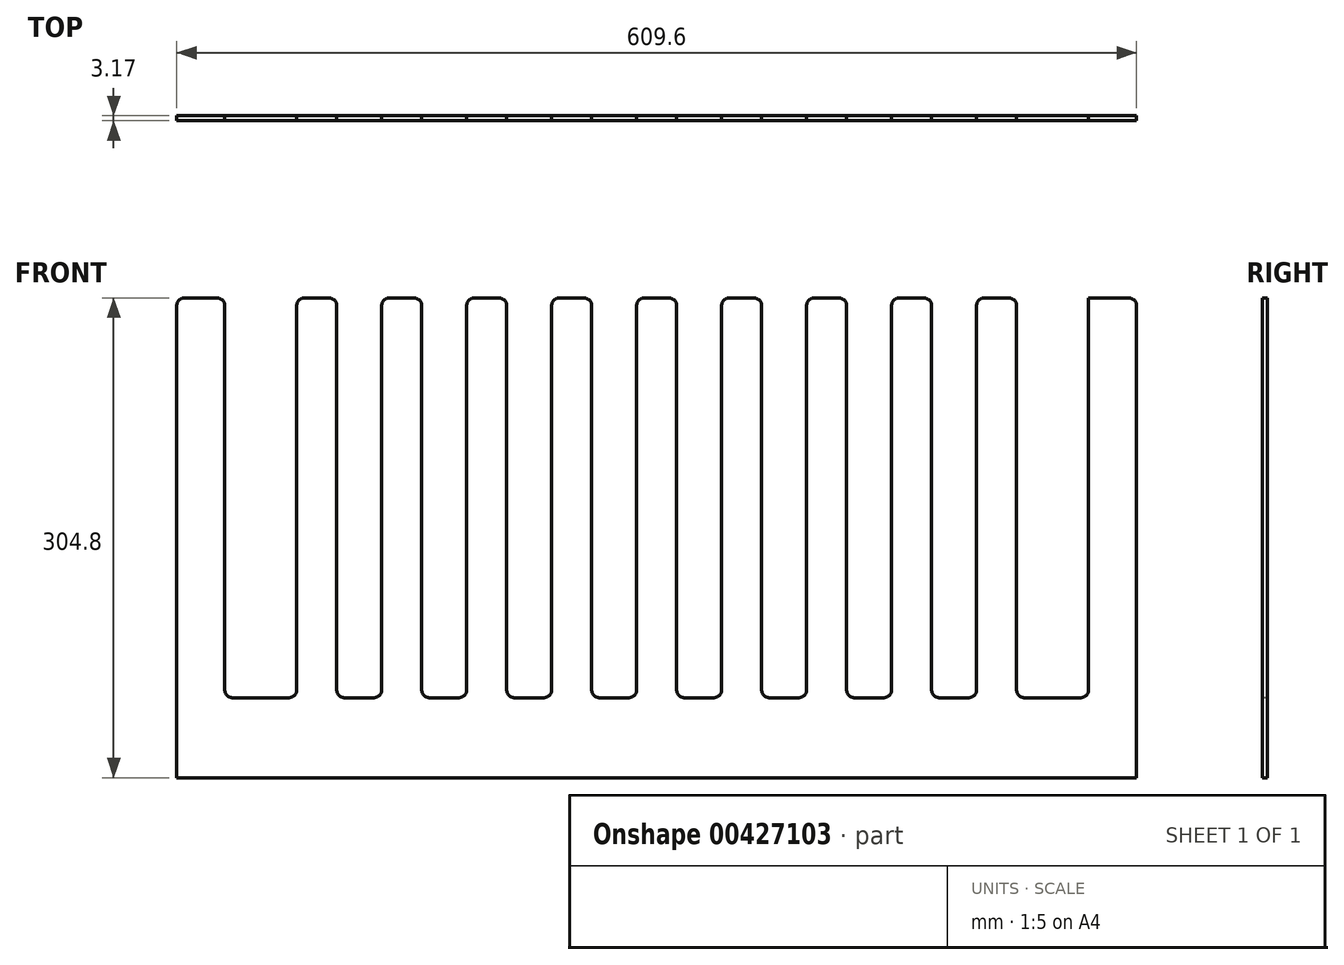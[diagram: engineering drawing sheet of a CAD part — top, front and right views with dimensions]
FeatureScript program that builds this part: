
annotation { "Feature Type Name" : "Feature", "Feature Type Description" : "" }
export const myFeature = defineFeature(function(context is Context, id is Id, definition is map)
    precondition{}
    {
        {
            var Q0;
            Q0=qCreatedBy(makeId("Front.planeOp"),FACE);
            var sketch = newSketch(context, id + "F0", { "sketchPlane" : qUnion([Q0])});
            skLineSegment(sketch, "E0.bottom", {"start": v(304.8, -152.4) * mm, "end": v(-304.8, -152.4) * mm});
            skLineSegment(sketch, "E0.top", {"start": v(304.8, 152.4) * mm, "end": v(-304.8, 152.4) * mm});
            skLineSegment(sketch, "E0.left", {"start": v(304.8, -152.4) * mm, "end": v(304.8, 152.4) * mm});
            skLineSegment(sketch, "E0.right", {"start": v(-304.8, -152.4) * mm, "end": v(-304.8, 152.4) * mm});
            skPoint(sketch, "E0.middle", {"position": v(0, 0) * mm});
            skSolve(sketch);
        }
        {
            var Q0;
            Q0=makeQuery(id+"F0.imprint","IMPRINT",FACE,{"disambiguationData":[TD([[makeQuery(id+"F0.imprint","IMPRINT",EDGE,{"derivedFrom":sQuery(id+"F0.wireOp",EDGE,"E0.bottom")}),-1.0]])]});
            extrude(context, id + "F1", {"entities" : qUnion([Q0]), "depth" : 3.17 * mm, "offsetDistance" : 25.4 * mm});
        }
        {
            var Q0;
            Q0=makeQuery(id+"F1.opExtrude","SWEPT_FACE",FACE,{"disambiguationData":[OSD([sQuery(id+"F0.wireOp",EDGE,"E0.top")])]});
            var sketch = newSketch(context, id + "F2", { "sketchPlane" : qUnion([Q0])});
            skLineSegment(sketch, "E1.bottom", {"start": v(-304.8, 0) * mm, "end": v(-274.32, 0) * mm});
            skLineSegment(sketch, "E1.top", {"start": v(-304.8, -3.18) * mm, "end": v(-274.32, -3.17) * mm});
            skLineSegment(sketch, "E1.left", {"start": v(-304.8, 0) * mm, "end": v(-304.8, -3.18) * mm});
            skLineSegment(sketch, "E1.right", {"start": v(-274.32, 0) * mm, "end": v(-274.32, -3.18) * mm});
            skLineSegment(sketch, "E2.bottom", {"start": v(-274.32, 0) * mm, "end": v(-228.6, 0) * mm});
            skLineSegment(sketch, "E2.top", {"start": v(-274.32, -3.18) * mm, "end": v(-228.6, -3.17) * mm});
            skLineSegment(sketch, "E2.right", {"start": v(-228.6, 0) * mm, "end": v(-228.6, -3.18) * mm});
            skLineSegment(sketch, "E3.bottom", {"start": v(-228.6, 0) * mm, "end": v(-203.2, 0) * mm});
            skLineSegment(sketch, "E3.top", {"start": v(-228.6, -3.18) * mm, "end": v(-203.2, -3.18) * mm});
            skLineSegment(sketch, "E3.right", {"start": v(-203.2, 0) * mm, "end": v(-203.2, -3.18) * mm});
            skLineSegment(sketch, "E4.bottom", {"start": v(-203.2, 0) * mm, "end": v(-174.62, 0) * mm});
            skLineSegment(sketch, "E4.top", {"start": v(-203.2, -3.18) * mm, "end": v(-174.62, -3.18) * mm});
            skLineSegment(sketch, "E4.right", {"start": v(-174.62, 0) * mm, "end": v(-174.62, -3.18) * mm});
            skLineSegment(sketch, "E5.bottom", {"start": v(-174.62, 0) * mm, "end": v(-149.22, 0) * mm});
            skLineSegment(sketch, "E5.top", {"start": v(-174.62, -3.17) * mm, "end": v(-149.22, -3.17) * mm});
            skLineSegment(sketch, "E5.right", {"start": v(-149.22, 0) * mm, "end": v(-149.22, -3.18) * mm});
            skLineSegment(sketch, "E6.bottom", {"start": v(-149.22, 0) * mm, "end": v(-120.65, 0) * mm});
            skLineSegment(sketch, "E6.top", {"start": v(-149.22, -3.18) * mm, "end": v(-120.65, -3.18) * mm});
            skLineSegment(sketch, "E6.right", {"start": v(-120.65, 0) * mm, "end": v(-120.65, -3.18) * mm});
            skLineSegment(sketch, "E7.bottom", {"start": v(-120.65, 0) * mm, "end": v(-95.25, 0) * mm});
            skLineSegment(sketch, "E7.top", {"start": v(-120.65, -3.18) * mm, "end": v(-95.25, -3.18) * mm});
            skLineSegment(sketch, "E7.right", {"start": v(-95.25, 0) * mm, "end": v(-95.25, -3.18) * mm});
            skLineSegment(sketch, "E8.bottom", {"start": v(-95.25, 0) * mm, "end": v(-66.67, 0) * mm});
            skLineSegment(sketch, "E8.top", {"start": v(-95.25, -3.18) * mm, "end": v(-66.67, -3.18) * mm});
            skLineSegment(sketch, "E8.right", {"start": v(-66.67, 0) * mm, "end": v(-66.67, -3.18) * mm});
            skLineSegment(sketch, "E9.bottom", {"start": v(-66.67, 0) * mm, "end": v(-41.27, 0) * mm});
            skLineSegment(sketch, "E9.top", {"start": v(-66.67, -3.18) * mm, "end": v(-41.27, -3.18) * mm});
            skLineSegment(sketch, "E9.right", {"start": v(-41.27, 0) * mm, "end": v(-41.27, -3.18) * mm});
            skLineSegment(sketch, "E10.bottom", {"start": v(-41.27, 0) * mm, "end": v(-12.7, 0) * mm});
            skLineSegment(sketch, "E10.top", {"start": v(-41.27, -3.18) * mm, "end": v(-12.7, -3.18) * mm});
            skLineSegment(sketch, "E10.right", {"start": v(-12.7, 0) * mm, "end": v(-12.7, -3.18) * mm});
            skLineSegment(sketch, "E11.bottom", {"start": v(-12.7, 0) * mm, "end": v(12.7, 0) * mm});
            skLineSegment(sketch, "E11.top", {"start": v(-12.7, -3.18) * mm, "end": v(12.7, -3.18) * mm});
            skLineSegment(sketch, "E11.right", {"start": v(12.7, 0) * mm, "end": v(12.7, -3.18) * mm});
            skLineSegment(sketch, "E12.bottom", {"start": v(12.7, 0) * mm, "end": v(41.28, 0) * mm});
            skLineSegment(sketch, "E12.top", {"start": v(12.7, -3.18) * mm, "end": v(41.28, -3.18) * mm});
            skLineSegment(sketch, "E12.right", {"start": v(41.28, 0) * mm, "end": v(41.28, -3.18) * mm});
            skLineSegment(sketch, "E13.bottom", {"start": v(41.28, 0) * mm, "end": v(66.68, 0) * mm});
            skLineSegment(sketch, "E13.top", {"start": v(41.28, -3.18) * mm, "end": v(66.68, -3.18) * mm});
            skLineSegment(sketch, "E13.right", {"start": v(66.68, 0) * mm, "end": v(66.68, -3.18) * mm});
            skLineSegment(sketch, "E14.bottom", {"start": v(66.68, 0) * mm, "end": v(95.25, 0) * mm});
            skLineSegment(sketch, "E14.top", {"start": v(66.68, -3.18) * mm, "end": v(95.25, -3.18) * mm});
            skLineSegment(sketch, "E14.right", {"start": v(95.25, 0) * mm, "end": v(95.25, -3.18) * mm});
            skLineSegment(sketch, "E15.bottom", {"start": v(95.25, 0) * mm, "end": v(120.65, 0) * mm});
            skLineSegment(sketch, "E15.top", {"start": v(95.25, -3.18) * mm, "end": v(120.65, -3.18) * mm});
            skLineSegment(sketch, "E15.right", {"start": v(120.65, 0) * mm, "end": v(120.65, -3.18) * mm});
            skLineSegment(sketch, "E16.bottom", {"start": v(120.65, 0) * mm, "end": v(149.23, 0) * mm});
            skLineSegment(sketch, "E16.top", {"start": v(120.65, -3.18) * mm, "end": v(149.23, -3.18) * mm});
            skLineSegment(sketch, "E16.right", {"start": v(149.23, 0) * mm, "end": v(149.23, -3.18) * mm});
            skLineSegment(sketch, "E17.bottom", {"start": v(149.23, 0) * mm, "end": v(174.63, 0) * mm});
            skLineSegment(sketch, "E17.top", {"start": v(149.23, -3.18) * mm, "end": v(174.63, -3.18) * mm});
            skLineSegment(sketch, "E17.right", {"start": v(174.63, 0) * mm, "end": v(174.63, -3.18) * mm});
            skLineSegment(sketch, "E18.bottom", {"start": v(174.63, 0) * mm, "end": v(203.2, 0) * mm});
            skLineSegment(sketch, "E18.top", {"start": v(174.63, -3.18) * mm, "end": v(203.2, -3.18) * mm});
            skLineSegment(sketch, "E18.right", {"start": v(203.2, 0) * mm, "end": v(203.2, -3.18) * mm});
            skLineSegment(sketch, "E19.bottom", {"start": v(203.2, 0) * mm, "end": v(228.6, 0) * mm});
            skLineSegment(sketch, "E19.top", {"start": v(203.2, -3.18) * mm, "end": v(228.6, -3.18) * mm});
            skLineSegment(sketch, "E19.right", {"start": v(228.6, 0) * mm, "end": v(228.6, -3.18) * mm});
            skLineSegment(sketch, "E20.bottom", {"start": v(228.6, 0) * mm, "end": v(274.32, 0) * mm});
            skLineSegment(sketch, "E20.top", {"start": v(228.6, -3.18) * mm, "end": v(274.32, -3.17) * mm});
            skLineSegment(sketch, "E20.right", {"start": v(274.32, 0) * mm, "end": v(274.32, -3.18) * mm});
            skLineSegment(sketch, "E21.bottom", {"start": v(274.32, 0) * mm, "end": v(304.8, 0) * mm});
            skLineSegment(sketch, "E21.top", {"start": v(274.32, -3.18) * mm, "end": v(304.8, -3.18) * mm});
            skLineSegment(sketch, "E21.right", {"start": v(304.8, 0) * mm, "end": v(304.8, -3.18) * mm});
            skSolve(sketch);
        }
        {
            var Q0;
            Q0=makeQuery(id+"F2.imprint","IMPRINT",FACE,{"disambiguationData":[TD([[makeQuery(id+"F2.imprint","IMPRINT",EDGE,{"derivedFrom":sQuery(id+"F2.wireOp",EDGE,"E2.bottom")}),1.0]])]});
            var Q1;
            Q1=makeQuery(id+"F2.imprint","IMPRINT",FACE,{"disambiguationData":[TD([[makeQuery(id+"F2.imprint","IMPRINT",EDGE,{"derivedFrom":sQuery(id+"F2.wireOp",EDGE,"E4.bottom")}),1.0]])]});
            var Q2;
            Q2=makeQuery(id+"F2.imprint","IMPRINT",FACE,{"disambiguationData":[TD([[makeQuery(id+"F2.imprint","IMPRINT",EDGE,{"derivedFrom":sQuery(id+"F2.wireOp",EDGE,"E6.bottom")}),1.0]])]});
            var Q3;
            Q3=makeQuery(id+"F2.imprint","IMPRINT",FACE,{"disambiguationData":[TD([[makeQuery(id+"F2.imprint","IMPRINT",EDGE,{"derivedFrom":sQuery(id+"F2.wireOp",EDGE,"E8.bottom")}),1.0]])]});
            var Q4;
            Q4=makeQuery(id+"F2.imprint","IMPRINT",FACE,{"disambiguationData":[TD([[makeQuery(id+"F2.imprint","IMPRINT",EDGE,{"derivedFrom":sQuery(id+"F2.wireOp",EDGE,"E10.bottom")}),1.0]])]});
            var Q5;
            Q5=makeQuery(id+"F2.imprint","IMPRINT",FACE,{"disambiguationData":[TD([[makeQuery(id+"F2.imprint","IMPRINT",EDGE,{"derivedFrom":sQuery(id+"F2.wireOp",EDGE,"E12.bottom")}),1.0]])]});
            var Q6;
            Q6=makeQuery(id+"F2.imprint","IMPRINT",FACE,{"disambiguationData":[TD([[makeQuery(id+"F2.imprint","IMPRINT",EDGE,{"derivedFrom":sQuery(id+"F2.wireOp",EDGE,"E14.bottom")}),1.0]])]});
            var Q7;
            Q7=makeQuery(id+"F2.imprint","IMPRINT",FACE,{"disambiguationData":[TD([[makeQuery(id+"F2.imprint","IMPRINT",EDGE,{"derivedFrom":sQuery(id+"F2.wireOp",EDGE,"E16.bottom")}),1.0]])]});
            var Q8;
            Q8=makeQuery(id+"F2.imprint","IMPRINT",FACE,{"disambiguationData":[TD([[makeQuery(id+"F2.imprint","IMPRINT",EDGE,{"derivedFrom":sQuery(id+"F2.wireOp",EDGE,"E18.bottom")}),1.0]])]});
            var Q9;
            Q9=makeQuery(id+"F2.imprint","IMPRINT",FACE,{"disambiguationData":[TD([[makeQuery(id+"F2.imprint","IMPRINT",EDGE,{"derivedFrom":sQuery(id+"F2.wireOp",EDGE,"E20.bottom")}),1.0]])]});
            extrude(context, id + "F3", {"entities" : qUnion([Q0, Q1, Q2, Q3, Q4, Q5, Q6, Q7, Q8, Q9]), "operationType" : NewBodyOperationType.REMOVE, "oppositeDirection" : true, "depth" : 254 * mm});
        }
        {
            var Q0;
            Q0=makeQuery(id+"F3.boolean.opBoolean","COPY",EDGE,{"derivedFrom":makeQuery(id+"F3.opExtrude","CAP_EDGE",EDGE,{"disambiguationData":[OSD([sQuery(id+"F2.wireOp",EDGE,"E1.right")])],"isStart":true})});
            var Q1;
            Q1=makeQuery(id+"F3.boolean.opBoolean","COPY",EDGE,{"derivedFrom":makeQuery(id+"F3.opExtrude","CAP_EDGE",EDGE,{"disambiguationData":[OSD([sQuery(id+"F2.wireOp",EDGE,"E2.right")])],"isStart":true})});
            var Q2;
            Q2=makeQuery(id+"F3.boolean.opBoolean","COPY",EDGE,{"derivedFrom":makeQuery(id+"F3.opExtrude","CAP_EDGE",EDGE,{"disambiguationData":[OSD([sQuery(id+"F2.wireOp",EDGE,"E2.right")])],"isStart":false})});
            var Q3;
            Q3=makeQuery(id+"F3.boolean.opBoolean","COPY",EDGE,{"derivedFrom":makeQuery(id+"F3.opExtrude","CAP_EDGE",EDGE,{"disambiguationData":[OSD([sQuery(id+"F2.wireOp",EDGE,"E1.right")])],"isStart":false})});
            var Q4;
            Q4=makeQuery(id+"F1.opExtrude","SWEPT_EDGE",EDGE,{"disambiguationData":[OSD([sQuery(id+"F0.wireOp",EDGE,"E0.top"),sQuery(id+"F0.wireOp",EDGE,"E0.right")])]});
            var Q5;
            Q5=makeQuery(id+"F1.opExtrude","SWEPT_EDGE",EDGE,{"disambiguationData":[OSD([sQuery(id+"F0.wireOp",EDGE,"E0.top"),sQuery(id+"F0.wireOp",EDGE,"E0.left")])]});
            var Q6;
            Q6=makeQuery(id+"F3.boolean.opBoolean","COPY",EDGE,{"derivedFrom":makeQuery(id+"F3.opExtrude","CAP_EDGE",EDGE,{"disambiguationData":[OSD([sQuery(id+"F2.wireOp",EDGE,"E2.right")])],"isStart":false})});
            var Q7;
            Q7=makeQuery(id+"F3.boolean.opBoolean","COPY",EDGE,{"derivedFrom":makeQuery(id+"F3.opExtrude","CAP_EDGE",EDGE,{"disambiguationData":[OSD([sQuery(id+"F2.wireOp",EDGE,"E3.right")])],"isStart":true})});
            var Q8;
            Q8=makeQuery(id+"F3.boolean.opBoolean","COPY",EDGE,{"derivedFrom":makeQuery(id+"F3.opExtrude","CAP_EDGE",EDGE,{"disambiguationData":[OSD([sQuery(id+"F2.wireOp",EDGE,"E4.right")])],"isStart":true})});
            var Q9;
            Q9=makeQuery(id+"F3.boolean.opBoolean","COPY",EDGE,{"derivedFrom":makeQuery(id+"F3.opExtrude","CAP_EDGE",EDGE,{"disambiguationData":[OSD([sQuery(id+"F2.wireOp",EDGE,"E5.right")])],"isStart":true})});
            var Q10;
            Q10=makeQuery(id+"F3.boolean.opBoolean","COPY",EDGE,{"derivedFrom":makeQuery(id+"F3.opExtrude","CAP_EDGE",EDGE,{"disambiguationData":[OSD([sQuery(id+"F2.wireOp",EDGE,"E6.right")])],"isStart":true})});
            var Q11;
            Q11=makeQuery(id+"F3.boolean.opBoolean","COPY",EDGE,{"derivedFrom":makeQuery(id+"F3.opExtrude","CAP_EDGE",EDGE,{"disambiguationData":[OSD([sQuery(id+"F2.wireOp",EDGE,"E7.right")])],"isStart":true})});
            var Q12;
            Q12=makeQuery(id+"F3.boolean.opBoolean","COPY",EDGE,{"derivedFrom":makeQuery(id+"F3.opExtrude","CAP_EDGE",EDGE,{"disambiguationData":[OSD([sQuery(id+"F2.wireOp",EDGE,"E8.right")])],"isStart":true})});
            var Q13;
            Q13=makeQuery(id+"F3.boolean.opBoolean","COPY",EDGE,{"derivedFrom":makeQuery(id+"F3.opExtrude","CAP_EDGE",EDGE,{"disambiguationData":[OSD([sQuery(id+"F2.wireOp",EDGE,"E9.right")])],"isStart":true})});
            var Q14;
            Q14=makeQuery(id+"F3.boolean.opBoolean","COPY",EDGE,{"derivedFrom":makeQuery(id+"F3.opExtrude","CAP_EDGE",EDGE,{"disambiguationData":[OSD([sQuery(id+"F2.wireOp",EDGE,"E10.right")])],"isStart":true})});
            var Q15;
            Q15=makeQuery(id+"F3.boolean.opBoolean","COPY",EDGE,{"derivedFrom":makeQuery(id+"F3.opExtrude","CAP_EDGE",EDGE,{"disambiguationData":[OSD([sQuery(id+"F2.wireOp",EDGE,"E11.right")])],"isStart":true})});
            var Q16;
            Q16=makeQuery(id+"F3.boolean.opBoolean","COPY",EDGE,{"derivedFrom":makeQuery(id+"F3.opExtrude","CAP_EDGE",EDGE,{"disambiguationData":[OSD([sQuery(id+"F2.wireOp",EDGE,"E13.right")])],"isStart":true})});
            var Q17;
            Q17=makeQuery(id+"F3.boolean.opBoolean","COPY",EDGE,{"derivedFrom":makeQuery(id+"F3.opExtrude","CAP_EDGE",EDGE,{"disambiguationData":[OSD([sQuery(id+"F2.wireOp",EDGE,"E14.right")])],"isStart":true})});
            var Q18;
            Q18=makeQuery(id+"F3.boolean.opBoolean","COPY",EDGE,{"derivedFrom":makeQuery(id+"F3.opExtrude","CAP_EDGE",EDGE,{"disambiguationData":[OSD([sQuery(id+"F2.wireOp",EDGE,"E16.right")])],"isStart":true})});
            var Q19;
            Q19=makeQuery(id+"F3.boolean.opBoolean","COPY",EDGE,{"derivedFrom":makeQuery(id+"F3.opExtrude","CAP_EDGE",EDGE,{"disambiguationData":[OSD([sQuery(id+"F2.wireOp",EDGE,"E12.right")])],"isStart":true})});
            var Q20;
            Q20=makeQuery(id+"F3.boolean.opBoolean","COPY",EDGE,{"derivedFrom":makeQuery(id+"F3.opExtrude","CAP_EDGE",EDGE,{"disambiguationData":[OSD([sQuery(id+"F2.wireOp",EDGE,"E15.right")])],"isStart":true})});
            var Q21;
            Q21=makeQuery(id+"F3.boolean.opBoolean","COPY",EDGE,{"derivedFrom":makeQuery(id+"F3.opExtrude","CAP_EDGE",EDGE,{"disambiguationData":[OSD([sQuery(id+"F2.wireOp",EDGE,"E17.right")])],"isStart":true})});
            var Q22;
            Q22=makeQuery(id+"F3.boolean.opBoolean","COPY",EDGE,{"derivedFrom":makeQuery(id+"F3.opExtrude","CAP_EDGE",EDGE,{"disambiguationData":[OSD([sQuery(id+"F2.wireOp",EDGE,"E2.right")])],"isStart":true})});
            var Q23;
            Q23=makeQuery(id+"F3.boolean.opBoolean","COPY",EDGE,{"derivedFrom":makeQuery(id+"F3.opExtrude","CAP_EDGE",EDGE,{"disambiguationData":[OSD([sQuery(id+"F2.wireOp",EDGE,"E19.right")])],"isStart":true})});
            var Q24;
            Q24=makeQuery(id+"F3.boolean.opBoolean","COPY",EDGE,{"derivedFrom":makeQuery(id+"F3.opExtrude","CAP_EDGE",EDGE,{"disambiguationData":[OSD([sQuery(id+"F2.wireOp",EDGE,"E20.right")])],"isStart":true})});
            var Q25;
            Q25=makeQuery(id+"F3.boolean.opBoolean","COPY",EDGE,{"derivedFrom":makeQuery(id+"F3.opExtrude","CAP_EDGE",EDGE,{"disambiguationData":[OSD([sQuery(id+"F2.wireOp",EDGE,"E18.right")])],"isStart":true})});
            fillet(context, id + "F4", {"entities" : qUnion([Q0, Q1, Q2, Q3, Q4, Q5, Q6, Q7, Q8, Q9, Q10, Q11, Q12, Q13, Q14, Q15, Q16, Q17, Q18, Q19, Q20, Q21, Q22, Q23, Q24, Q25]), "radius" : 5.08 * mm, "tangentPropagation" : true, "allowEdgeOverflow" : false});
        }
        {
            var Q0;
            Q0=makeQuery(id+"F3.boolean.opBoolean","COPY",EDGE,{"derivedFrom":makeQuery(id+"F3.opExtrude","CAP_EDGE",EDGE,{"disambiguationData":[OSD([sQuery(id+"F2.wireOp",EDGE,"E4.right")])],"isStart":false})});
            var Q1;
            Q1=makeQuery(id+"F3.boolean.opBoolean","COPY",EDGE,{"derivedFrom":makeQuery(id+"F3.opExtrude","CAP_EDGE",EDGE,{"disambiguationData":[OSD([sQuery(id+"F2.wireOp",EDGE,"E6.right")])],"isStart":false})});
            var Q2;
            Q2=makeQuery(id+"F3.boolean.opBoolean","COPY",EDGE,{"derivedFrom":makeQuery(id+"F3.opExtrude","CAP_EDGE",EDGE,{"disambiguationData":[OSD([sQuery(id+"F2.wireOp",EDGE,"E8.right")])],"isStart":false})});
            var Q3;
            Q3=makeQuery(id+"F3.boolean.opBoolean","COPY",EDGE,{"derivedFrom":makeQuery(id+"F3.opExtrude","CAP_EDGE",EDGE,{"disambiguationData":[OSD([sQuery(id+"F2.wireOp",EDGE,"E10.right")])],"isStart":false})});
            var Q4;
            Q4=makeQuery(id+"F3.boolean.opBoolean","COPY",EDGE,{"derivedFrom":makeQuery(id+"F3.opExtrude","CAP_EDGE",EDGE,{"disambiguationData":[OSD([sQuery(id+"F2.wireOp",EDGE,"E12.right")])],"isStart":false})});
            var Q5;
            Q5=makeQuery(id+"F3.boolean.opBoolean","COPY",EDGE,{"derivedFrom":makeQuery(id+"F3.opExtrude","CAP_EDGE",EDGE,{"disambiguationData":[OSD([sQuery(id+"F2.wireOp",EDGE,"E14.right")])],"isStart":false})});
            var Q6;
            Q6=makeQuery(id+"F3.boolean.opBoolean","COPY",EDGE,{"derivedFrom":makeQuery(id+"F3.opExtrude","CAP_EDGE",EDGE,{"disambiguationData":[OSD([sQuery(id+"F2.wireOp",EDGE,"E16.right")])],"isStart":false})});
            var Q7;
            Q7=makeQuery(id+"F3.boolean.opBoolean","COPY",EDGE,{"derivedFrom":makeQuery(id+"F3.opExtrude","CAP_EDGE",EDGE,{"disambiguationData":[OSD([sQuery(id+"F2.wireOp",EDGE,"E18.right")])],"isStart":false})});
            var Q8;
            Q8=makeQuery(id+"F3.boolean.opBoolean","COPY",EDGE,{"derivedFrom":makeQuery(id+"F3.opExtrude","CAP_EDGE",EDGE,{"disambiguationData":[OSD([sQuery(id+"F2.wireOp",EDGE,"E20.right")])],"isStart":false})});
            var Q9;
            Q9=makeQuery(id+"F3.boolean.opBoolean","COPY",EDGE,{"derivedFrom":makeQuery(id+"F3.opExtrude","CAP_EDGE",EDGE,{"disambiguationData":[OSD([sQuery(id+"F2.wireOp",EDGE,"E19.right")])],"isStart":false})});
            var Q10;
            Q10=makeQuery(id+"F3.boolean.opBoolean","COPY",EDGE,{"derivedFrom":makeQuery(id+"F3.opExtrude","CAP_EDGE",EDGE,{"disambiguationData":[OSD([sQuery(id+"F2.wireOp",EDGE,"E17.right")])],"isStart":false})});
            var Q11;
            Q11=makeQuery(id+"F3.boolean.opBoolean","COPY",EDGE,{"derivedFrom":makeQuery(id+"F3.opExtrude","CAP_EDGE",EDGE,{"disambiguationData":[OSD([sQuery(id+"F2.wireOp",EDGE,"E15.right")])],"isStart":false})});
            var Q12;
            Q12=makeQuery(id+"F3.boolean.opBoolean","COPY",EDGE,{"derivedFrom":makeQuery(id+"F3.opExtrude","CAP_EDGE",EDGE,{"disambiguationData":[OSD([sQuery(id+"F2.wireOp",EDGE,"E13.right")])],"isStart":false})});
            var Q13;
            Q13=makeQuery(id+"F3.boolean.opBoolean","COPY",EDGE,{"derivedFrom":makeQuery(id+"F3.opExtrude","CAP_EDGE",EDGE,{"disambiguationData":[OSD([sQuery(id+"F2.wireOp",EDGE,"E11.right")])],"isStart":false})});
            var Q14;
            Q14=makeQuery(id+"F3.boolean.opBoolean","COPY",EDGE,{"derivedFrom":makeQuery(id+"F3.opExtrude","CAP_EDGE",EDGE,{"disambiguationData":[OSD([sQuery(id+"F2.wireOp",EDGE,"E9.right")])],"isStart":false})});
            var Q15;
            Q15=makeQuery(id+"F3.boolean.opBoolean","COPY",EDGE,{"derivedFrom":makeQuery(id+"F3.opExtrude","CAP_EDGE",EDGE,{"disambiguationData":[OSD([sQuery(id+"F2.wireOp",EDGE,"E7.right")])],"isStart":false})});
            var Q16;
            Q16=makeQuery(id+"F3.boolean.opBoolean","COPY",EDGE,{"derivedFrom":makeQuery(id+"F3.opExtrude","CAP_EDGE",EDGE,{"disambiguationData":[OSD([sQuery(id+"F2.wireOp",EDGE,"E5.right")])],"isStart":false})});
            var Q17;
            Q17=makeQuery(id+"F3.boolean.opBoolean","COPY",EDGE,{"derivedFrom":makeQuery(id+"F3.opExtrude","CAP_EDGE",EDGE,{"disambiguationData":[OSD([sQuery(id+"F2.wireOp",EDGE,"E3.right")])],"isStart":false})});
            fillet(context, id + "F5", {"entities" : qUnion([Q0, Q1, Q2, Q3, Q4, Q5, Q6, Q7, Q8, Q9, Q10, Q11, Q12, Q13, Q14, Q15, Q16, Q17]), "radius" : 5.08 * mm, "tangentPropagation" : true, "allowEdgeOverflow" : false});
        }
    });
